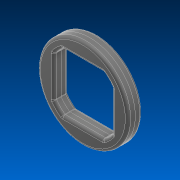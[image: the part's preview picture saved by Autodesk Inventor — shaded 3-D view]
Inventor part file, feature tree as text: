
AUTODESK INVENTOR PART (.ipt)
format: ipt  version: 2022.2 (Build 262287000, 287)  size: 203,776 bytes
history: native  units: in
note: dims shown in document units (in); Inventor stores cm internally (conversion verified against a paired STEP export)
features: fillet x1
ambient origin geometry x8: Origin, YZ Plane, XZ Plane, XY Plane, X Axis, Y Axis, Z Axis, Center Point
bodies: Solid1 (feature_tree)
feature tree (1):
  fillet  "Fillet1"  [1 undecoded]
note: 1 required parameter value undecoded (feature->parameter linkage not recoverable at this tier; creation-order binding heuristic only, values carry confidence <= 0.55)
